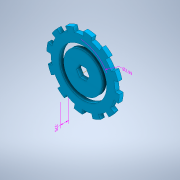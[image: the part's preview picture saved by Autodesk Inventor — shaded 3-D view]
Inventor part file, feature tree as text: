
AUTODESK INVENTOR PART (.ipt)
format: ipt  version: 2021.2 (Build 252289000, 289)  size: 979,456 bytes
history: native  units: in
note: dims shown in document units (in); Inventor stores cm internally (conversion verified against a paired STEP export)
features: sketch x5, extrude x4, other x3, pattern_circular x1, revolve x1, split x1
ambient origin geometry x8: Origin, YZ Plane, XZ Plane, XY Plane, X Axis, Y Axis, Z Axis, Center Point
bodies: Solid1 (feature_tree)
feature tree (15):
  other  "Annotations"
  extrude  "Extrusion1"  Depth=0.375in TaperAngle=0.0deg
  extrude  "Extrusion11"  TaperAngle=0.0deg  [1 undecoded]
  extrude  "Extrusion19"  Depth=0.0069in
  pattern_circular  "Circular Pattern11"  [2 undecoded]
  extrude  "Extrusion26"  Depth=4.7244in
  revolve  "Revolution2"  Angle=360.0deg
  split  "Split2"
  sketch  "Sketch1"  dims[d0=2.985in d1=0.375in d2=0.0in]
  sketch  "Sketch10"  dims[d55=0.515in d56=0.0in d57=0.0in]
  sketch  "Sketch17"  dims[d123=0.1963in d124=0.0069in]
  sketch  "Sketch28"  dims[d125=0.0893in]
  sketch  "Sketch34"  dims[d126=0.375in d127=0.0in d128=4.7244in d129=360.0deg d131=2.985in d132=3.3777in d181=2.25in d182=0.05in d183=0.0in d203=0.2in d204=0.1in d205=1.0in d206=0.4in d207=0.125in d208=90.0deg d136=0.375in d184=0.237in d185=2.985in]
  other  "Linear Dimension 2"
  other  "Diameter Dimension 1"
note: 3 required parameter values undecoded (feature->parameter linkage not recoverable at this tier; creation-order binding heuristic only, values carry confidence <= 0.55)
